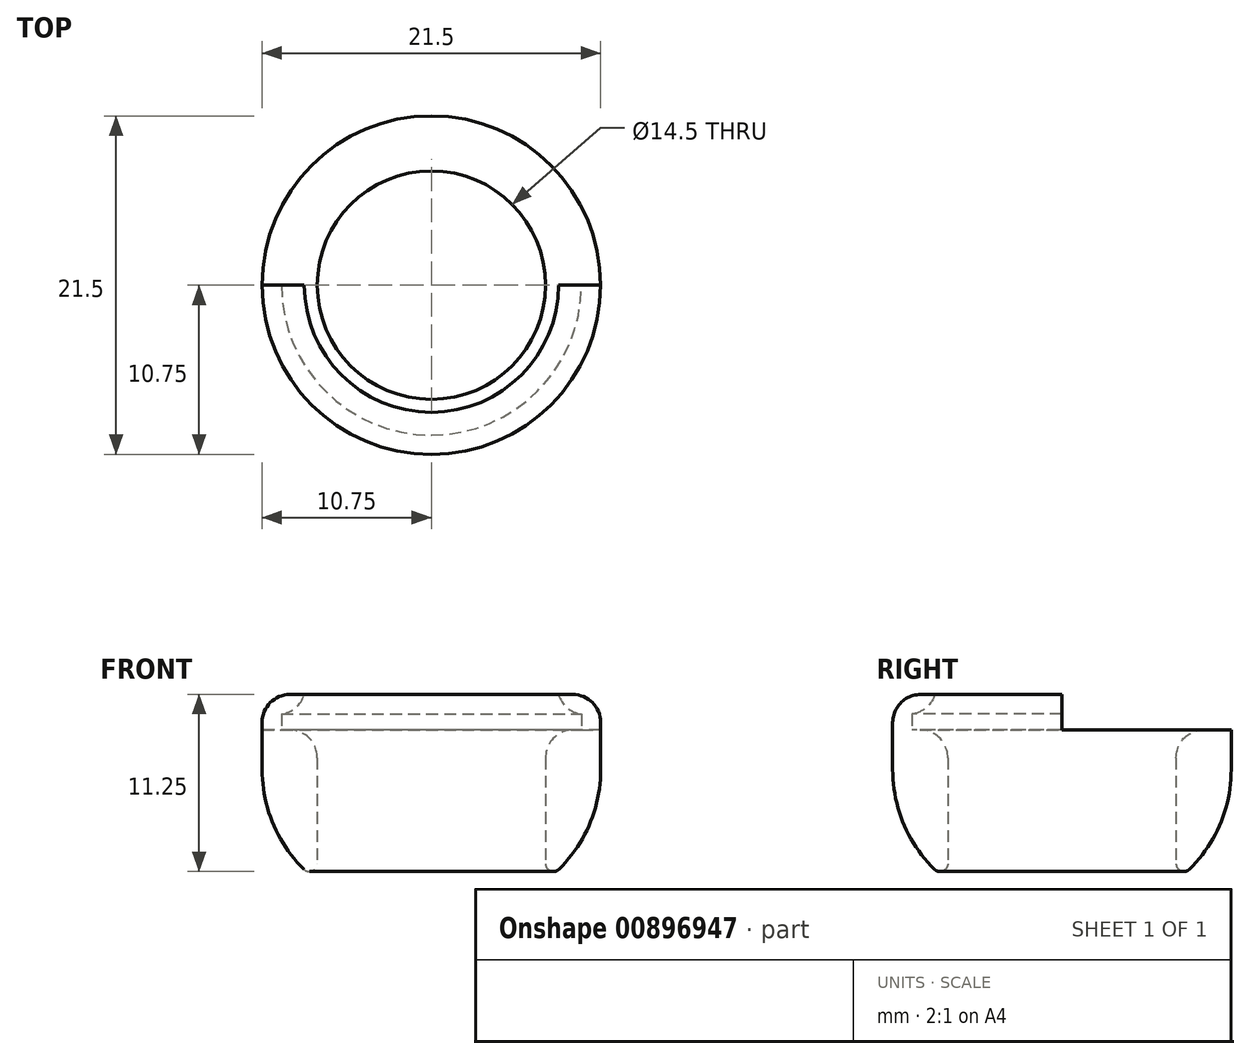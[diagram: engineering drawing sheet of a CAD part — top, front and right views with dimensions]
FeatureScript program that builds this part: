
annotation { "Feature Type Name" : "Feature", "Feature Type Description" : "" }
export const myFeature = defineFeature(function(context is Context, id is Id, definition is map)
    precondition{}
    {
        {
            var Q0;
            Q0=qCreatedBy(makeId("Top.planeOp"),FACE);
            var sketch = newSketch(context, id + "F0", { "sketchPlane" : qUnion([Q0])});
            skCircle(sketch, "E0", {"center": v(0, 0) * mm, "radius": 10.75 * mm});
            skCircle(sketch, "E1", {"center": v(0, 0) * mm, "radius": 7.25 * mm});
            skSolve(sketch);
        }
        {
            var Q0;
            Q0 = qSketchRegion(id + "F0", true);
            extrude(context, id + "F1", {"entities" : qUnion([Q0]), "depth" : (1.3 + .8 + 7.5) * mm, "offsetDistance" : 25.4 * mm});
        }
        {
            var Q0;
            Q0=makeQuery(id+"F1.opExtrude","CAP_FACE",FACE,{"disambiguationData":[OSD([sQuery(id+"F0.wireOp",EDGE,"E0"),sQuery(id+"F0.wireOp",EDGE,"E1")])],"isStart":false});
            var sketch = newSketch(context, id + "F2", { "sketchPlane" : qUnion([Q0])});
            skCircle(sketch, "E2", {"center": v(0, 0) * mm, "radius": 10.75 * mm});
            skCircle(sketch, "E3", {"center": v(0, 0) * mm, "radius": 8.25 * mm});
            skCircle(sketch, "E4", {"center": v(0, 0) * mm, "radius": 9.53 * mm});
            skSolve(sketch);
        }
        {
            var Q0;
            Q0=makeQuery(id+"F2.imprint","IMPRINT",FACE,{"disambiguationData":[TD([[makeQuery(id+"F2.imprint","IMPRINT",EDGE,{"derivedFrom":sQuery(id+"F2.wireOp",EDGE,"E2")}),1.0]])]});
            var sketch = newSketch(context, id + "F3", { "sketchPlane" : qUnion([Q0])});
            skLineSegment(sketch, "E5.bottom", {"start": v(-12.88, 0) * mm, "end": v(12.65, 0) * mm});
            skLineSegment(sketch, "E5.top", {"start": v(-12.88, -11.5) * mm, "end": v(12.65, -11.5) * mm});
            skLineSegment(sketch, "E5.left", {"start": v(-12.88, 0) * mm, "end": v(-12.88, -11.5) * mm});
            skLineSegment(sketch, "E5.right", {"start": v(12.65, 0) * mm, "end": v(12.65, -11.5) * mm});
            skSolve(sketch);
        }
        {
            var Q0;
            {var subQ0=sQuery(id+"F3.wireOp",EDGE,"E5.bottom");var subQ1=makeQuery(id+"F2.imprint","IMPRINT",EDGE,{"derivedFrom":sQuery(id+"F2.wireOp",EDGE,"E2")});var subQ2=makeQuery(id+"F3.imprint","INTERSECT",VERTEX,{"disambiguationData":[OD(0.0)],"derivedFrom":[subQ1,subQ0]});Q0=makeQuery(id+"F3.imprint","IMPRINT",FACE,{"disambiguationData":[TD([[makeQuery(id+"F3.imprint","IMPRINT",EDGE,{"disambiguationData":[TD([[subQ2,-1.0]])],"derivedFrom":subQ0}),-1.0]])]});}
            extrude(context, id + "F4", {"entities" : qUnion([Q0]), "operationType" : NewBodyOperationType.ADD, "depth" : (1.39 + .85) * mm, "offsetDistance" : 25.4 * mm});
        }
        {
            var Q0;
            Q0=makeQuery(id+"F4.opExtrude","CAP_FACE",FACE,{"disambiguationData":[OSD([sQuery(id+"F2.wireOp",EDGE,"E2"),sQuery(id+"F2.wireOp",EDGE,"E4"),sQuery(id+"F3.wireOp",EDGE,"E5.bottom")])],"isStart":false});
            var sketch = newSketch(context, id + "F5", { "sketchPlane" : qUnion([Q0])});
            skCircle(sketch, "E6", {"center": v(0, 0) * mm, "radius": 9.53 * mm});
            skCircle(sketch, "E7", {"center": v(0, 0) * mm, "radius": 8 * mm});
            skLineSegment(sketch, "E8.bottom", {"start": v(-13.44, 0) * mm, "end": v(13.8, 0) * mm});
            skLineSegment(sketch, "E8.top", {"start": v(-13.44, -13.14) * mm, "end": v(13.8, -13.14) * mm});
            skLineSegment(sketch, "E8.left", {"start": v(-13.44, 0) * mm, "end": v(-13.44, -13.14) * mm});
            skLineSegment(sketch, "E8.right", {"start": v(13.8, 0) * mm, "end": v(13.8, -13.14) * mm});
            skSolve(sketch);
        }
        {
            var Q0;
            {var subQ0=sQuery(id+"F5.wireOp",EDGE,"E8.bottom");var subQ1=sQuery(id+"F5.wireOp",EDGE,"E6");var subQ2=makeQuery(id+"F5.imprint","INTERSECT",VERTEX,{"disambiguationData":[OD(0.0)],"derivedFrom":[subQ1,subQ0]});Q0=makeQuery(id+"F5.imprint","IMPRINT",FACE,{"disambiguationData":[TD([[makeQuery(id+"F5.imprint","IMPRINT",EDGE,{"disambiguationData":[TD([[subQ2,-1.0]])],"derivedFrom":subQ1}),1.0]])]});}
            extrude(context, id + "F6", {"entities" : qUnion([Q0]), "operationType" : NewBodyOperationType.ADD, "oppositeDirection" : true, "depth" : 1.25 * mm, "offsetDistance" : 25.4 * mm});
        }
        {
            var Q0;
            Q0=makeQuery(id+"F6.opExtrude","CAP_EDGE",EDGE,{"disambiguationData":[OSD([sQuery(id+"F5.wireOp",EDGE,"E7")])],"isStart":false});
            var Q1;
            Q1=makeQuery(id+"F1.opExtrude","CAP_EDGE",EDGE,{"disambiguationData":[OSD([sQuery(id+"F0.wireOp",EDGE,"E1")])],"isStart":false});
            var Q2;
            Q2=makeQuery(id+"F4.opExtrude","CAP_EDGE",EDGE,{"disambiguationData":[OSD([sQuery(id+"F2.wireOp",EDGE,"E2")])],"isStart":false});
            fillet(context, id + "F7", {"entities" : qUnion([Q0, Q1, Q2]), "radius" : 1.78 * mm, "allowEdgeOverflow" : false});
        }
        {
            var Q0;
            Q0=makeQuery(id+"F1.opExtrude","CAP_EDGE",EDGE,{"disambiguationData":[OSD([sQuery(id+"F0.wireOp",EDGE,"E0")])],"isStart":true});
            fillet(context, id + "F8", {"entities" : qUnion([Q0]), "radius" : 8.9 * mm, "tangentPropagation" : true, "allowEdgeOverflow" : false});
        }
        {
            var Q0;
            Q0=makeQuery(id+"F8.opFillet","BLEND_EDGE",EDGE,{"blendedFrom":[makeQuery(id+"F1.opExtrude","CAP_EDGE",EDGE,{"disambiguationData":[OSD([sQuery(id+"F0.wireOp",EDGE,"E0")])],"isStart":true}),makeQuery(id+"F1.opExtrude","SWEPT_FACE",FACE,{"disambiguationData":[OSD([sQuery(id+"F0.wireOp",EDGE,"E1")])]})],"blendedInto":[makeQuery(id+"F1.opExtrude","SWEPT_FACE",FACE,{"disambiguationData":[OSD([sQuery(id+"F0.wireOp",EDGE,"E1")])]})]});
            fillet(context, id + "F9", {"entities" : qUnion([Q0]), "radius" : .5 * mm, "tangentPropagation" : true, "allowEdgeOverflow" : false});
        }
    });
